FCSTD DOCUMENT  (FreeCAD 0.19R23578 (Git))
Label: frame_assembly
License: All rights reserved
LicenseURL: http://en.wikipedia.org/wiki/All_rights_reserved
objects: App::Link×11, App::DocumentObjectGroup×2, PartDesign::CoordinateSystem×1, App::FeaturePython×1, App::Part×1
note: 1 computed .brp shape members not serialized (recipe doc carries the construction recipe); baked Part::Feature solids carry a one-line shape summary decoded from their .brp
EXTERNAL_REF file=frame_bottom_piece.FCStd obj=LCS_4
EXTERNAL_REF file=frame_bottom_piece.FCStd obj=Part008
EXTERNAL_REF file=frame_bottom_piece.FCStd obj=LCS_2
EXTERNAL_REF file=frame_side_piece.FCStd obj=LCS_2
EXTERNAL_REF file=frame_side_piece.FCStd obj=Part006
EXTERNAL_REF file=frame_bottom_piece.FCStd obj=LCS_1
EXTERNAL_REF file=frame_side_piece.FCStd obj=LCS_1
EXTERNAL_REF file=frame_top_piece.FCStd obj=LCS_2
EXTERNAL_REF file=frame_top_piece.FCStd obj=Part007
EXTERNAL_REF file=frame_top_piece.FCStd obj=LCS_3
EXTERNAL_REF file=z_motor_adaptor_plate.FCStd obj=LCS_1
EXTERNAL_REF file=z_motor_adaptor_plate.FCStd obj=Part
EXTERNAL_REF file=Nema 17  Stepper Motor length 60mm.FcStd obj=LCS_0
EXTERNAL_REF file=z_motor_adaptor_plate.FCStd obj=LCS_2
EXTERNAL_REF file=Nema 17  Stepper Motor length 60mm.FcStd obj=Part
EXTERNAL_REF file=Nema 17  Stepper Motor length 60mm.FcStd obj=LCS_1
EXTERNAL_REF file=5to8mm_spider_coupler.FCStd obj=LCS_1
EXTERNAL_REF file=5to8mm_spider_coupler.FCStd obj=CouplerASM
EXTERNAL_REF file=T8_leadscrew_l388mm.FCStd obj=LCS_1
EXTERNAL_REF file=T8_leadscrew_l388mm.FCStd obj=Part
EXTERNAL_REF file=KLF08_bearing_block.FCStd obj=LCS_1
EXTERNAL_REF file=frame_bottom_piece.FCStd obj=LCS_3
EXTERNAL_REF file=KLF08_bearing_block.FCStd obj=Part
EXTERNAL_REF file=12x500mm_linear_shaft.FCStd obj=LCS_1
EXTERNAL_REF file=frame_bottom_piece.FCStd obj=LCS_5
EXTERNAL_REF file=12x500mm_linear_shaft.FCStd obj=Part
EXTERNAL_REF file=frame_bottom_piece.FCStd obj=LCS_6

FEATURE [App::DocumentObjectGroup] Parts
FEATURE [PartDesign::CoordinateSystem] LCS_Origin
  AttacherType = Attacher::AttachEngine3D
  MapMode = 2
  Support = -> [X_Axis]
FEATURE [App::DocumentObjectGroup] Constraints
FEATURE [App::FeaturePython] Variables  # WARN: FeaturePython — macro-defined, semantics opaque (R4)
FEATURE [App::Link] frame_bottom_piece_frame_bottom_piece
  AssemblyType = Asm4EE
  AttachedBy = #LCS_4
  AttachedTo = Parent Assembly#LCS_Origin
  LinkPlacement = pos=(-25.4,0,0) rot=(0,0,1;0rad)
  LinkedObject = -> <external frame_bottom_piece.FCStd>#Part008
  Placement = pos=(-25.4,0,0) rot=(0,0,1;0rad)
  expr: Placement = LCS_Origin.Placement * AttachmentOffset * frame_bottom_piece#LCS_4.Placement ^ -1
FEATURE [App::Link] frame_side_piece_frame_side_piece
  AssemblyType = Asm4EE
  AttachedBy = #LCS_2
  AttachedTo = frame_bottom_piece_frame_bottom_piece#LCS_2
  AttachmentOffset = pos=(0,0,0) rot=(1,0,0;4.71239rad)
  LinkPlacement = pos=(25.4,127,50.8) rot=(0,0,-1;4.71239rad)
  LinkedObject = -> <external frame_side_piece.FCStd>#Part006
  Placement = pos=(25.4,127,50.8) rot=(0,0,-1;4.71239rad)
  expr: Placement = frame_bottom_piece_frame_bottom_piece.Placement * frame_bottom_piece#LCS_2.Placement * AttachmentOffset * frame_side_piece#LCS_2.Placement ^ -1
FEATURE [App::Link] frame_side_piece_frame_side_piece_2
  AssemblyType = Asm4EE
  AttachedBy = #LCS_2
  AttachedTo = frame_bottom_piece_frame_bottom_piece#LCS_1
  AttachmentOffset = pos=(0,0,0) rot=(1,0,0;4.71239rad)
  LinkPlacement = pos=(25.4,-177.8,50.8) rot=(0,0,-1;4.71239rad)
  LinkedObject = -> <external frame_side_piece.FCStd>#Part006
  Placement = pos=(25.4,-177.8,50.8) rot=(0,0,-1;4.71239rad)
  expr: Placement = frame_bottom_piece_frame_bottom_piece.Placement * frame_bottom_piece#LCS_1.Placement * AttachmentOffset * frame_side_piece#LCS_2.Placement ^ -1
FEATURE [App::Link] frame_top_piece_frame_top_piece
  AssemblyType = Asm4EE
  AttachedBy = #LCS_2
  AttachedTo = frame_side_piece_frame_side_piece#LCS_1
  AttachmentOffset = pos=(0,0,0) rot=(1,0,0;1.5708rad)
  LinkPlacement = pos=(-25.4,-5.68e-14,449.2) rot=(0,0,1;0rad)
  LinkedObject = -> <external frame_top_piece.FCStd>#Part007
  Placement = pos=(-25.4,-5.68e-14,449.2) rot=(0,0,1;0rad)
  expr: Placement = frame_side_piece_frame_side_piece.Placement * frame_side_piece#LCS_1.Placement * AttachmentOffset * frame_top_piece#LCS_2.Placement ^ -1
FEATURE [App::Link] z_motor_adaptor_plate_z_motor_adaptor_plate
  AssemblyType = Asm4EE
  AttachedBy = #LCS_1
  AttachedTo = frame_top_piece_frame_top_piece#LCS_3
  AttachmentOffset = pos=(0,0,0) rot=(0,0,1;4.71239rad)
  LinkPlacement = pos=(-2.238e-13,-5.68e-14,500) rot=(0,0,-1;1.5708rad)
  LinkedObject = -> <external z_motor_adaptor_plate.FCStd>#Part
  Placement = pos=(-2.238e-13,-5.68e-14,500) rot=(0,0,-1;1.5708rad)
  expr: Placement = frame_top_piece_frame_top_piece.Placement * frame_top_piece#LCS_3.Placement * AttachmentOffset * z_motor_adaptor_plate#LCS_1.Placement ^ -1
FEATURE [App::Link] Nema_17__Stepper_Motor_length_60mm_Nema_17__Stepper_Motor_length_60mm  label="Nema_17__Stepper_Motor_length_60mm_Nema 17  Stepper Motor length 60mm"
  AssemblyType = Asm4EE
  AttachedBy = #LCS_0
  AttachedTo = z_motor_adaptor_plate_z_motor_adaptor_plate#LCS_2
  AttachmentOffset = pos=(0,0,0) rot=(1,0,0;3.14159rad)
  LinkPlacement = pos=(-2.804e-13,-6.32e-14,565.75) rot=(1,0,0;1.5708rad)
  LinkedObject = -> <external Nema 17  Stepper Motor length 60mm.FcStd>#Part
  Placement = pos=(-2.804e-13,-6.32e-14,565.75) rot=(1,0,0;1.5708rad)
  expr: Placement = z_motor_adaptor_plate_z_motor_adaptor_plate.Placement * z_motor_adaptor_plate#LCS_2.Placement * AttachmentOffset * Nema_17__Stepper_Motor_length_60mm#LCS_0.Placement ^ -1
FEATURE [App::Link] _to8mm_spider_coupler_5to8mm_spider_coupler
  AssemblyType = Asm4EE
  AttachedBy = #LCS_1
  AttachedTo = Nema_17__Stepper_Motor_length_60mm_Nema_17__Stepper_Motor_length_60mm#LCS_1
  AttachmentOffset = pos=(0,0,0) rot=(0,1,0;3.14159rad)
  LinkPlacement = pos=(-2.101e-13,-4.47e-14,497.15) rot=(-0.085794,-0.7045,0.7045;2.97042rad)
  LinkedObject = -> <external 5to8mm_spider_coupler.FCStd>#CouplerASM
  Placement = pos=(-2.101e-13,-4.47e-14,497.15) rot=(-0.085794,-0.7045,0.7045;2.97042rad)
  expr: Placement = Nema_17__Stepper_Motor_length_60mm_Nema_17__Stepper_Motor_length_60mm.Placement * Nema_17__Stepper_Motor_length_60mm#LCS_1.Placement * AttachmentOffset * _to8mm_spider_coupler#LCS_1.Placement ^ -1
FEATURE [App::Link] T8_leadscrew_l388mm_T8_leadscrew_l388mm
  AssemblyType = Asm4EE
  AttachedBy = #LCS_1
  AttachedTo = _to8mm_spider_coupler_5to8mm_spider_coupler#LCS_1
  AttachmentOffset = pos=(0,0,0) rot=(0,-1,0;3.14159rad)
  LinkPlacement = pos=(-2.051e-13,-4.55e-14,482.15) rot=(0.707107,0.707107,0;3.14159rad)
  LinkedObject = -> <external T8_leadscrew_l388mm.FCStd>#Part
  Placement = pos=(-2.051e-13,-4.55e-14,482.15) rot=(0.707107,0.707107,0;3.14159rad)
  expr: Placement = _to8mm_spider_coupler_5to8mm_spider_coupler.Placement * _to8mm_spider_coupler#LCS_1.Placement * AttachmentOffset * T8_leadscrew_l388mm#LCS_1.Placement ^ -1
FEATURE [App::Link] KLF08_bearing_block_KLF08
  AssemblyType = Asm4EE
  AttachedBy = #LCS_1
  AttachedTo = frame_bottom_piece_frame_bottom_piece#LCS_3
  AttachmentOffset = pos=(0,0,0) rot=(1,0,0;3.14159rad)
  LinkPlacement = pos=(0,0,50.8) rot=(0.57735,0.57735,0.57735;2.0944rad)
  LinkedObject = -> <external KLF08_bearing_block.FCStd>#Part
  Placement = pos=(0,0,50.8) rot=(0.57735,0.57735,0.57735;2.0944rad)
  expr: Placement = frame_bottom_piece_frame_bottom_piece.Placement * frame_bottom_piece#LCS_3.Placement * AttachmentOffset * KLF08_bearing_block#LCS_1.Placement ^ -1
FEATURE [App::Link] _2x500mm_linear_shaft_12x500mm_linear_shaft
  AssemblyType = Asm4EE
  AttachedBy = #LCS_1
  AttachedTo = frame_bottom_piece_frame_bottom_piece#LCS_5
  LinkPlacement = pos=(13.4,-95.25,0) rot=(0,0,-1;1.5708rad)
  LinkedObject = -> <external 12x500mm_linear_shaft.FCStd>#Part
  Placement = pos=(13.4,-95.25,0) rot=(0,0,-1;1.5708rad)
  expr: Placement = frame_bottom_piece_frame_bottom_piece.Placement * frame_bottom_piece#LCS_5.Placement * AttachmentOffset * _2x500mm_linear_shaft#LCS_1.Placement ^ -1
FEATURE [App::Link] _2x500mm_linear_shaft_12x500mm_linear_shaft_2
  AssemblyType = Asm4EE
  AttachedBy = #LCS_1
  AttachedTo = frame_bottom_piece_frame_bottom_piece#LCS_6
  LinkPlacement = pos=(13.4,95.25,0) rot=(0,0,-1;1.5708rad)
  LinkedObject = -> <external 12x500mm_linear_shaft.FCStd>#Part
  Placement = pos=(13.4,95.25,0) rot=(0,0,-1;1.5708rad)
  expr: Placement = frame_bottom_piece_frame_bottom_piece.Placement * frame_bottom_piece#LCS_6.Placement * AttachmentOffset * _2x500mm_linear_shaft#LCS_1.Placement ^ -1
FEATURE [App::Part] Model
  Configuration = 0
  Group = -> [LCS_Origin,Constraints,Variables,frame_bottom_piece_frame_bottom_piece,frame_side_piece_frame_side_piece,frame_side_piece_frame_side_piece_2,frame_top_piece_frame_top_piece,z_motor_adaptor_plate_z_motor_adaptor_plate,Nema_17__Stepper_Motor_length_60mm_Nema_17__Stepper_Motor_length_60mm,_to8mm_spider_coupler_5to8mm_spider_coupler,T8_leadscrew_l388mm_T8_leadscrew_l388mm,KLF08_bearing_block_KLF08,+2 more]
  Origin = -> Origin
  Type = Assembly4 Model

RESOLVED EXTERNAL PARTS (link-assembly join: the EXTERNAL_REF files above that resolve inside this repo's crawl, each included once):
---- part 12x500mm_linear_shaft.FCStd = doc fcstd_1ea531625638 ----
FCSTD DOCUMENT  (FreeCAD 0.19R23578 (Git))
Label: 12x500mm_linear_shaft
License: All rights reserved
LicenseURL: http://en.wikipedia.org/wiki/All_rights_reserved
objects: Sketcher::SketchObject×1, PartDesign::Pad×1, PartDesign::Chamfer×1, PartDesign::Body×1, PartDesign::CoordinateSystem×1, App::Part×1
note: 7 computed .brp shape members not serialized (recipe doc carries the construction recipe); baked Part::Feature solids carry a one-line shape summary decoded from their .brp

FEATURE [Sketcher::SketchObject] Sketch
  MapMode = 5
  Support = -> [XY_Plane001]
  sketch-geometry (1):
    g0: Circle CenterX=0 CenterY=0 CenterZ=0 NormalX=0 NormalY=0 NormalZ=1 AngleXU=0 Radius=6
  constraints (2):
    c: Coincident(g0,g-1)
    c: Diameter(g0) = 12
FEATURE [PartDesign::Pad] Pad
  Direction = (1,1,1)
  Length = 500
  Length2 = 100
  Profile = -> Sketch
  Type = 0
FEATURE [PartDesign::Chamfer] Chamfer
  Angle = 45
  Base = -> Pad [Edge2,Edge3]
  BaseFeature = -> Pad
  ChamferType = 0
  FlipDirection = false
  Size = 1
  Size2 = 1
  SupportTransform = true
FEATURE [PartDesign::Body] Body
  Group = -> [Sketch,Pad,Chamfer]
  Origin = -> Origin001
  Tip = -> Chamfer
FEATURE [PartDesign::CoordinateSystem] LCS_1
  AttacherType = Attacher::AttachEngine3D
  MapMode = 11
  Placement = pos=(0,0,0) rot=(0,0,1;1.5708rad)
  Support = -> [Chamfer]
FEATURE [App::Part] Part  label="12x500mm_linear_shaft"
  Group = -> [Body,LCS_1]
  Origin = -> Origin
---- part T8_leadscrew_l388mm.FCStd = doc fcstd_92d1f95667da ----
FCSTD DOCUMENT  (FreeCAD 0.19R23578 (Git))
Label: T8_leadscrew_l388mm
License: All rights reserved
LicenseURL: http://en.wikipedia.org/wiki/All_rights_reserved
objects: PartDesign::CoordinateSystem×2, Sketcher::SketchObject×1, PartDesign::Pad×1, PartDesign::Chamfer×1, PartDesign::Body×1, App::Part×1
note: 8 computed .brp shape members not serialized (recipe doc carries the construction recipe); baked Part::Feature solids carry a one-line shape summary decoded from their .brp

FEATURE [Sketcher::SketchObject] Sketch
  MapMode = 5
  Support = -> [XY_Plane001]
  sketch-geometry (1):
    g0: Circle CenterX=0 CenterY=0 CenterZ=0 NormalX=0 NormalY=0 NormalZ=1 AngleXU=0 Radius=4
  constraints (2):
    c: Coincident(g0,g-1)
    c: Diameter(g0) = 8
FEATURE [PartDesign::Pad] Pad
  Direction = (1,1,1)
  Length = 433
  Length2 = 100
  Profile = -> Sketch
  Type = 0
FEATURE [PartDesign::Chamfer] Chamfer
  Angle = 45
  Base = -> Pad [Edge2,Edge3]
  BaseFeature = -> Pad
  ChamferType = 0
  FlipDirection = false
  Size = 1
  Size2 = 1
  SupportTransform = true
FEATURE [PartDesign::Body] Body
  Group = -> [Sketch,Pad,Chamfer]
  Origin = -> Origin001
  Tip = -> Chamfer
FEATURE [PartDesign::CoordinateSystem] LCS_1
  AttacherType = Attacher::AttachEngine3D
  MapMode = 11
  Placement = pos=(0,0,0) rot=(0,0,1;1.5708rad)
  Support = -> [Chamfer]
FEATURE [PartDesign::CoordinateSystem] LCS_2
  AttacherType = Attacher::AttachEngine3D
  MapMode = 45
  Placement = pos=(-9e-16,-1e-16,216.5) rot=(0,0,1;0rad)
  Support = -> [Chamfer]
FEATURE [App::Part] Part  label="T8_leadscrew_l388mm"
  Group = -> [Body,LCS_1,LCS_2]
  Origin = -> Origin
---- part frame_bottom_piece.FCStd = doc fcstd_ccebaa61afa7 ----
FCSTD DOCUMENT  (FreeCAD 0.19R23578 (Git))
Label: frame_bottom_piece
License: All rights reserved
LicenseURL: http://en.wikipedia.org/wiki/All_rights_reserved
objects: PartDesign::CoordinateSystem×6, Sketcher::SketchObject×4, PartDesign::Pocket×3, PartDesign::Pad×1, PartDesign::Body×1, App::Part×1
note: 19 computed .brp shape members not serialized (recipe doc carries the construction recipe); baked Part::Feature solids carry a one-line shape summary decoded from their .brp

FEATURE [Sketcher::SketchObject] Sketch006
  AttachmentOffset = pos=(0,0,50.8) rot=(0,0,1;0rad)
  MapMode = 5
  Placement = pos=(50.8,-1.13e-14,1.13e-14) rot=(0.57735,0.57735,0.57735;2.0944rad)
  Support = -> [YZ_Plane011]
  sketch-geometry (8):
    g0: ArcOfCircle CenterX=-131 CenterY=25.4 CenterZ=0 NormalX=0 NormalY=0 NormalZ=1 AngleXU=0 Radius=5 StartAngle=1.5708 EndAngle=4.71239
    g1: ArcOfCircle CenterX=-95 CenterY=25.4 CenterZ=0 NormalX=0 NormalY=0 NormalZ=1 AngleXU=0 Radius=5 StartAngle=4.71239 EndAngle=7.85398
    g2: LineSegment StartX=-131 StartY=20.4 StartZ=0 EndX=-95 EndY=20.4 EndZ=0
    g3: LineSegment StartX=-131 StartY=30.4 StartZ=0 EndX=-95 EndY=30.4 EndZ=0
    g4: ArcOfCircle CenterX=95 CenterY=25.4 CenterZ=0 NormalX=0 NormalY=0 NormalZ=1 AngleXU=0 Radius=5 StartAngle=1.5708 EndAngle=4.71239
    g5: ArcOfCircle CenterX=131 CenterY=25.4 CenterZ=0 NormalX=0 NormalY=0 NormalZ=1 AngleXU=0 Radius=5 StartAngle=4.71239 EndAngle=7.85398
    g6: LineSegment StartX=95 StartY=20.4 StartZ=0 EndX=131 EndY=20.4 EndZ=0
    g7: LineSegment StartX=95 StartY=30.4 StartZ=0 EndX=131 EndY=30.4 EndZ=0
  constraints (18):
    c: Tangent(g0,g3) = 1.5708
    c: Tangent(g0,g2) = -1.5708
    c: Tangent(g2,g1) = -1.5708
    c: Tangent(g3,g1) = 1.5708
    c: Horizontal(g2)
    c: Equal(g0,g1)
    c: Tangent(g4,g7) = 1.5708
    c: Tangent(g4,g6) = -1.5708
    c: Tangent(g6,g5) = -1.5708
    c: Tangent(g7,g5) = 1.5708
    c: Horizontal(g6)
    c: Diameter(g4) = 10
    c: Equal(g4,g1)
    c: Symmetric(g4,g1,g-2)
    c: Symmetric(g0,g5,g-2)
    c: DistanceY(g-1,g4) = 25.4
    c: DistanceX(g1,g4) = 190
    c: DistanceX(g0,g5) = 262
FEATURE [Sketcher::SketchObject] Sketch012
  AttachmentOffset = pos=(0,0,50.8) rot=(0,0,1;0rad)
  MapMode = 5
  Placement = pos=(0,0,50.8) rot=(0,0,1;0rad)
  Support = -> [XY_Plane011]
  sketch-geometry (4):
    g0: Circle CenterX=25.4 CenterY=0 CenterZ=0 NormalX=0 NormalY=0 NormalZ=1 AngleXU=0 Radius=9
    g1: Circle CenterX=25.4 CenterY=18.5 CenterZ=0 NormalX=0 NormalY=0 NormalZ=1 AngleXU=0 Radius=2.25
    g2: Circle CenterX=25.4 CenterY=-18.5 CenterZ=0 NormalX=0 NormalY=0 NormalZ=1 AngleXU=0 Radius=2.25
    g3: LineSegment StartX=25.4 StartY=18.5 StartZ=0 EndX=25.4 EndY=-18.5 EndZ=0
  constraints (10):
    c: PointOnObject(g0,g-1)
    c: Coincident(g3,g1)
    c: Coincident(g3,g2)
    c: PointOnObject(g0,g3)
    c: Symmetric(g1,g2,g-1)
    c: Equal(g1,g2)
    c: DistanceY(g2,g1) = 37
    c: DistanceX(g-1,g0) = 25.4
    c: Diameter(g1) = 4.5
    c: Diameter(g0) = 18
FEATURE [Sketcher::SketchObject] Sketch
  MapMode = 5
  Placement = pos=(0,0,0) rot=(1,0,0;1.5708rad)
  Support = -> [XZ_Plane011]
  sketch-geometry (16):
    g0: LineSegment StartX=10 StartY=0 StartZ=0 EndX=40.8 EndY=0 EndZ=0
    g1: LineSegment StartX=50.8 StartY=10 StartZ=0 EndX=50.8 EndY=40.8 EndZ=0
    g2: LineSegment StartX=40.8 StartY=50.8 StartZ=0 EndX=10 EndY=50.8 EndZ=0
    g3: LineSegment StartX=0 StartY=40.8 StartZ=0 EndX=0 EndY=10 EndZ=0
    g4: ArcOfCircle CenterX=10 CenterY=40.8 CenterZ=0 NormalX=0 NormalY=0 NormalZ=1 AngleXU=0 Radius=10 StartAngle=1.5708 EndAngle=3.14159
    g5: ArcOfCircle CenterX=10 CenterY=10 CenterZ=0 NormalX=0 NormalY=0 NormalZ=1 AngleXU=0 Radius=10 StartAngle=3.14159 EndAngle=4.71239
    g6: ArcOfCircle CenterX=40.8 CenterY=10 CenterZ=0 NormalX=0 NormalY=0 NormalZ=1 AngleXU=0 Radius=10 StartAngle=4.71239 EndAngle=6.28319
    g7: ArcOfCircle CenterX=40.8 CenterY=40.8 CenterZ=0 NormalX=0 NormalY=0 NormalZ=1 AngleXU=0 Radius=10 StartAngle=3e-16 EndAngle=1.5708
    g8: LineSegment StartX=10 StartY=46.0375 StartZ=0 EndX=40.8 EndY=46.0375 EndZ=0
    g9: LineSegment StartX=46.0375 StartY=40.8 StartZ=0 EndX=46.0375 EndY=10 EndZ=0
    g10: LineSegment StartX=40.8 StartY=4.7625 StartZ=0 EndX=10 EndY=4.7625 EndZ=0
    g11: LineSegment StartX=4.7625 StartY=10 StartZ=0 EndX=4.7625 EndY=40.8 EndZ=0
    g12: ArcOfCircle CenterX=10 CenterY=40.8 CenterZ=0 NormalX=0 NormalY=0 NormalZ=1 AngleXU=0 Radius=5.2375 StartAngle=1.5708 EndAngle=3.14159
    g13: ArcOfCircle CenterX=10 CenterY=10 CenterZ=0 NormalX=0 NormalY=0 NormalZ=1 AngleXU=0 Radius=5.2375 StartAngle=3.14159 EndAngle=4.71239
    g14: ArcOfCircle CenterX=40.8 CenterY=10 CenterZ=0 NormalX=0 NormalY=0 NormalZ=1 AngleXU=0 Radius=5.2375 StartAngle=4.71239 EndAngle=6.28319
    g15: ArcOfCircle CenterX=40.8 CenterY=40.8 CenterZ=0 NormalX=0 NormalY=0 NormalZ=1 AngleXU=0 Radius=5.2375 StartAngle=0 EndAngle=1.5708
  constraints (36):
    c: Horizontal(g0)
    c: Horizontal(g2)
    c: Vertical(g1)
    c: Vertical(g3)
    c: Tangent(g2,g4) = -1.5708
    c: Tangent(g3,g4) = -1.5708
    c: Tangent(g3,g5) = -1.5708
    c: Tangent(g0,g5) = -1.5708
    c: Tangent(g0,g6) = -1.5708
    c: Tangent(g1,g6) = -1.5708
    c: Tangent(g2,g7) = -1.5708
    c: Tangent(g1,g7) = -1.5708
    c: Horizontal(g8)
    c: Horizontal(g10)
    c: Vertical(g9)
    c: Tangent(g8,g12) = 1.5708
    c: Tangent(g11,g12) = 1.5708
    c: Tangent(g11,g13) = 1.5708
    c: Tangent(g10,g13) = 1.5708
    c: Tangent(g9,g14) = 1.5708
    c: Tangent(g10,g14) = 1.5708
    c: Tangent(g8,g15) = 1.5708
    c: Tangent(g9,g15) = 1.5708
    c: PointOnObject(g3,g-2)
    c: PointOnObject(g0,g-1)
    c: DistanceX(g3,g1) = 50.8
    c: DistanceY(g0,g2) = 50.8
    c: Coincident(g13,g5)
    c: Coincident(g12,g4)
    c: Coincident(g7,g15)
    c: Coincident(g14,g6)
    c: Equal(g5,g4)
    c: Equal(g4,g7)
    c: Equal(g7,g6)
    c: DistanceX(g3,g11) = 4.7625
    c: DistanceX(g3,g0) = 10
FEATURE [PartDesign::Pad] Pad
  AllowMultiFace = false
  Direction = (1,1,1)
  Length = 355.6
  Length2 = 100
  Midplane = true
  Placement = pos=(0,0,0) rot=(1,0,0;1.5708rad)
  Profile = -> Sketch
  Type = 0
FEATURE [Sketcher::SketchObject] Sketch005
  AttachmentOffset = pos=(0,0,50.8) rot=(0,0,1;0rad)
  MapMode = 5
  Placement = pos=(0,0,50.8) rot=(0,0,1;0rad)
  Support = -> [XY_Plane011]
  sketch-geometry (8):
    g0: LineSegment StartX=32.8 StartY=89.25 StartZ=0 EndX=57.8 EndY=89.25 EndZ=0
    g1: LineSegment StartX=57.8 StartY=89.25 StartZ=0 EndX=57.8 EndY=109.25 EndZ=0
    g2: LineSegment StartX=57.8 StartY=109.25 StartZ=0 EndX=32.8 EndY=109.25 EndZ=0
    g3: LineSegment StartX=32.8 StartY=109.25 StartZ=0 EndX=32.8 EndY=89.25 EndZ=0
    g4: LineSegment StartX=32.8 StartY=-89.25 StartZ=0 EndX=57.8 EndY=-89.25 EndZ=0
    g5: LineSegment StartX=57.8 StartY=-89.25 StartZ=0 EndX=57.8 EndY=-109.25 EndZ=0
    g6: LineSegment StartX=57.8 StartY=-109.25 StartZ=0 EndX=32.8 EndY=-109.25 EndZ=0
    g7: LineSegment StartX=32.8 StartY=-109.25 StartZ=0 EndX=32.8 EndY=-89.25 EndZ=0
  constraints (22):
    c: Coincident(g0,g1)
    c: Coincident(g1,g2)
    c: Coincident(g2,g3)
    c: Coincident(g3,g0)
    c: Horizontal(g0)
    c: Horizontal(g2)
    c: Vertical(g1)
    c: Vertical(g3)
    c: Coincident(g4,g5)
    c: Coincident(g5,g6)
    c: Coincident(g6,g7)
    c: Coincident(g7,g4)
    c: Horizontal(g4)
    c: Horizontal(g6)
    c: Vertical(g5)
    c: Vertical(g7)
    c: Symmetric(g0,g4,g-1)
    c: Symmetric(g1,g5,g-1)
    c: DistanceY(g1,g1) = 20
    c: DistanceX(g-1,g0) = 32.8
    c: DistanceX(g0,g0) = 25
    c: DistanceY(g4,g0) = 178.5
FEATURE [PartDesign::Pocket] Pocket
  AllowMultiFace = false
  BaseFeature = -> Pad
  Length = 5
  Length2 = 100
  Placement = pos=(0,0,0) rot=(1,0,0;1.5708rad)
  Profile = -> Sketch005
  Type = 1
FEATURE [PartDesign::Pocket] Pocket001
  AllowMultiFace = false
  BaseFeature = -> Pocket
  Length = 5
  Length2 = 100
  Placement = pos=(0,0,0) rot=(1,0,0;1.5708rad)
  Profile = -> Sketch006
  Type = 2
FEATURE [PartDesign::Pocket] Pocket006
  AllowMultiFace = false
  BaseFeature = -> Pocket001
  Length = 5
  Length2 = 100
  Placement = pos=(0,0,0) rot=(1,0,0;1.5708rad)
  Profile = -> Sketch012
  Type = 0
FEATURE [PartDesign::Body] Body
  Group = -> [Sketch,Pad,Sketch005,Pocket,Sketch006,Pocket001,Sketch012,Pocket006]
  Origin = -> Origin011
  Tip = -> Pocket006
FEATURE [PartDesign::CoordinateSystem] LCS_1
  AttacherType = Attacher::AttachEngine3D
  AttachmentOffset = pos=(25.4,0,0) rot=(0,0,1;0rad)
  MapMode = 45
  Placement = pos=(25.4,-152.4,50.8) rot=(0.57735,0.57735,0.57735;2.0944rad)
  Support = -> [Pocket006]
  expr: .AttachmentOffset.Base.x = 1"
FEATURE [PartDesign::CoordinateSystem] LCS_2
  AttacherType = Attacher::AttachEngine3D
  AttachmentOffset = pos=(-25.4,0,0) rot=(0,0,1;0rad)
  MapMode = 45
  Placement = pos=(25.4,152.4,50.8) rot=(0.57735,0.57735,0.57735;2.0944rad)
  Support = -> [Pocket006]
  expr: .AttachmentOffset.Base.x = -1"
FEATURE [PartDesign::CoordinateSystem] LCS_3
  AttacherType = Attacher::AttachEngine3D
  MapMode = 11
  Placement = pos=(25.4,0,50.8) rot=(0,0,1;1.5708rad)
  Support = -> [Pocket006]
FEATURE [PartDesign::CoordinateSystem] LCS_4
  AttacherType = Attacher::AttachEngine3D
  MapMode = 45
  Placement = pos=(25.4,0,0) rot=(0,0,1;0rad)
  Support = -> [Pocket006]
FEATURE [PartDesign::CoordinateSystem] LCS_5
  AttacherType = Attacher::AttachEngine3D
  AttachmentOffset = pos=(6,-6,0) rot=(0,0,1;0rad)
  MapMode = 1
  Placement = pos=(38.8,-95.25,0) rot=(0,0,1;0rad)
  Support = -> [Pocket006]
FEATURE [PartDesign::CoordinateSystem] LCS_6
  AttacherType = Attacher::AttachEngine3D
  AttachmentOffset = pos=(6,6,0) rot=(0,0,1;0rad)
  MapMode = 1
  Placement = pos=(38.8,95.25,0) rot=(0,0,1;0rad)
  Support = -> [Pocket006]
FEATURE [App::Part] Part008  label="frame_bottom_piece"
  Group = -> [Body,LCS_1,LCS_2,LCS_3,LCS_4,LCS_5,LCS_6]
  Origin = -> Origin009
---- part frame_side_piece.FCStd = doc fcstd_32cf0ac6b02a ----
FCSTD DOCUMENT  (FreeCAD 0.19R23578 (Git))
Label: frame_side_piece
License: All rights reserved
LicenseURL: http://en.wikipedia.org/wiki/All_rights_reserved
objects: PartDesign::CoordinateSystem×2, Sketcher::SketchObject×1, PartDesign::Pad×1, PartDesign::Body×1, App::Part×1
note: 6 computed .brp shape members not serialized (recipe doc carries the construction recipe); baked Part::Feature solids carry a one-line shape summary decoded from their .brp

FEATURE [Sketcher::SketchObject] Sketch004
  MapMode = 5
  sketch-geometry (16):
    g0: LineSegment StartX=10 StartY=0 StartZ=0 EndX=40.8 EndY=0 EndZ=0
    g1: LineSegment StartX=50.8 StartY=10 StartZ=0 EndX=50.8 EndY=40.8 EndZ=0
    g2: LineSegment StartX=40.8 StartY=50.8 StartZ=0 EndX=10 EndY=50.8 EndZ=0
    g3: LineSegment StartX=0 StartY=40.8 StartZ=0 EndX=0 EndY=10 EndZ=0
    g4: ArcOfCircle CenterX=10 CenterY=40.8 CenterZ=0 NormalX=0 NormalY=0 NormalZ=1 AngleXU=0 Radius=10 StartAngle=1.5708 EndAngle=3.14159
    g5: ArcOfCircle CenterX=10 CenterY=10 CenterZ=0 NormalX=0 NormalY=0 NormalZ=1 AngleXU=0 Radius=10 StartAngle=3.14159 EndAngle=4.71239
    g6: ArcOfCircle CenterX=40.8 CenterY=10 CenterZ=0 NormalX=0 NormalY=0 NormalZ=1 AngleXU=0 Radius=10 StartAngle=4.71239 EndAngle=6.28319
    g7: ArcOfCircle CenterX=40.8 CenterY=40.8 CenterZ=0 NormalX=0 NormalY=0 NormalZ=1 AngleXU=0 Radius=10 StartAngle=0 EndAngle=1.5708
    g8: LineSegment StartX=10 StartY=46.0375 StartZ=0 EndX=40.8 EndY=46.0375 EndZ=0
    g9: LineSegment StartX=46.0375 StartY=40.8 StartZ=0 EndX=46.0375 EndY=10 EndZ=0
    g10: LineSegment StartX=40.8 StartY=4.7625 StartZ=0 EndX=10 EndY=4.7625 EndZ=0
    g11: LineSegment StartX=4.7625 StartY=10 StartZ=0 EndX=4.7625 EndY=40.8 EndZ=0
    g12: ArcOfCircle CenterX=10 CenterY=40.8 CenterZ=0 NormalX=0 NormalY=0 NormalZ=1 AngleXU=0 Radius=5.2375 StartAngle=1.5708 EndAngle=3.14159
    g13: ArcOfCircle CenterX=10 CenterY=10 CenterZ=0 NormalX=0 NormalY=0 NormalZ=1 AngleXU=0 Radius=5.2375 StartAngle=3.14159 EndAngle=4.71239
    g14: ArcOfCircle CenterX=40.8 CenterY=10 CenterZ=0 NormalX=0 NormalY=0 NormalZ=1 AngleXU=0 Radius=5.2375 StartAngle=4.71239 EndAngle=6.28319
    g15: ArcOfCircle CenterX=40.8 CenterY=40.8 CenterZ=0 NormalX=0 NormalY=0 NormalZ=1 AngleXU=0 Radius=5.2375 StartAngle=4e-16 EndAngle=1.5708
  constraints (36):
    c: Horizontal(g0)
    c: Horizontal(g2)
    c: Vertical(g1)
    c: Vertical(g3)
    c: Tangent(g2,g4) = -1.5708
    c: Tangent(g3,g4) = -1.5708
    c: Tangent(g3,g5) = -1.5708
    c: Tangent(g0,g5) = -1.5708
    c: Tangent(g0,g6) = -1.5708
    c: Tangent(g1,g6) = -1.5708
    c: Tangent(g2,g7) = -1.5708
    c: Tangent(g1,g7) = -1.5708
    c: Horizontal(g8)
    c: Horizontal(g10)
    c: Vertical(g9)
    c: Tangent(g8,g12) = 1.5708
    c: Tangent(g11,g12) = 1.5708
    c: Tangent(g11,g13) = 1.5708
    c: Tangent(g10,g13) = 1.5708
    c: Tangent(g9,g14) = 1.5708
    c: Tangent(g10,g14) = 1.5708
    c: Tangent(g8,g15) = 1.5708
    c: Tangent(g9,g15) = 1.5708
    c: PointOnObject(g3,g-2)
    c: PointOnObject(g0,g-1)
    c: DistanceX(g3,g1) = 50.8
    c: DistanceY(g0,g2) = 50.8
    c: Coincident(g13,g5)
    c: Coincident(g12,g4)
    c: Coincident(g7,g15)
    c: Coincident(g14,g6)
    c: Equal(g5,g4)
    c: Equal(g4,g7)
    c: Equal(g7,g6)
    c: DistanceX(g3,g0) = 10
    c: DistanceX(g9,g1) = 4.7625
FEATURE [PartDesign::Pad] Pad004
  AllowMultiFace = false
  Direction = (1,1,1)
  Length = 398.4
  Length2 = 100
  Profile = -> Sketch004
  Type = 0
FEATURE [PartDesign::Body] Body004
  Group = -> [Sketch004,Pad004]
  Tip = -> Pad004
FEATURE [PartDesign::CoordinateSystem] LCS_1
  AttacherType = Attacher::AttachEngine3D
  MapMode = 45
  Placement = pos=(25.4,25.4,398.4) rot=(0,0,1;0rad)
  Support = -> [Pad004]
FEATURE [PartDesign::CoordinateSystem] LCS_2
  AttacherType = Attacher::AttachEngine3D
  MapMode = 45
  Placement = pos=(25.4,25.4,0) rot=(0,0,1;0rad)
  Support = -> [Pad004]
FEATURE [App::Part] Part006  label="frame_side_piece"
  Group = -> [Body004,LCS_1,LCS_2]
  Origin = -> Origin007
---- part frame_top_piece.FCStd = doc fcstd_cebd3a7141f0 ----
FCSTD DOCUMENT  (FreeCAD 0.19R23578 (Git))
Label: frame_top_piece
License: All rights reserved
LicenseURL: http://en.wikipedia.org/wiki/All_rights_reserved
objects: Sketcher::SketchObject×5, PartDesign::Pocket×4, PartDesign::CoordinateSystem×3, PartDesign::Pad×1, PartDesign::Body×1, App::Part×1
note: 19 computed .brp shape members not serialized (recipe doc carries the construction recipe); baked Part::Feature solids carry a one-line shape summary decoded from their .brp

FEATURE [Sketcher::SketchObject] Sketch010
  AttachmentOffset = pos=(0,0,50.8) rot=(0,0,1;0rad)
  MapMode = 5
  Placement = pos=(0,0,50.8) rot=(0,0,1;0rad)
  Support = -> [XY_Plane010]
  expr: Constraints[9] = (2 * 31 ^ 2) ^ 0.5
  sketch-geometry (4):
    g0: Circle CenterX=25.4 CenterY=0 CenterZ=0 NormalX=0 NormalY=0 NormalZ=1 AngleXU=0 Radius=11
    g1: Circle CenterX=25.4 CenterY=21.9203 CenterZ=0 NormalX=0 NormalY=0 NormalZ=1 AngleXU=0 Radius=1.55
    g2: Circle CenterX=25.4 CenterY=-21.9203 CenterZ=0 NormalX=0 NormalY=0 NormalZ=1 AngleXU=0 Radius=1.55
    g3: LineSegment StartX=25.4 StartY=21.9203 StartZ=0 EndX=25.4 EndY=-21.9203 EndZ=0
  constraints (10):
    c: PointOnObject(g0,g-1)
    c: Coincident(g3,g1)
    c: Coincident(g3,g2)
    c: DistanceX(g-1,g0) = 25.4
    c: PointOnObject(g0,g3)
    c: Symmetric(g1,g2,g-1)
    c: Equal(g1,g2)
    c: Diameter(g1) = 3.1
    c: Diameter(g0) = 22
    c: DistanceY(g2,g1) = 43.8406
FEATURE [Sketcher::SketchObject] Sketch011
  MapMode = 5
  Placement = pos=(0,0,0) rot=(0.57735,0.57735,0.57735;2.0944rad)
  Support = -> [YZ_Plane008]
  sketch-geometry (4):
    g0: LineSegment StartX=-20 StartY=20 StartZ=0 EndX=20 EndY=20 EndZ=0
    g1: LineSegment StartX=20 StartY=20 StartZ=0 EndX=20 EndY=-5 EndZ=0
    g2: LineSegment StartX=20 StartY=-5 StartZ=0 EndX=-20 EndY=-5 EndZ=0
    g3: LineSegment StartX=-20 StartY=-5 StartZ=0 EndX=-20 EndY=20 EndZ=0
  constraints (12):
    c: Coincident(g0,g1)
    c: Coincident(g1,g2)
    c: Coincident(g2,g3)
    c: Coincident(g3,g0)
    c: Horizontal(g0)
    c: Horizontal(g2)
    c: Vertical(g1)
    c: Vertical(g3)
    c: DistanceX(g0,g0) = 40
    c: DistanceY(g1,g0) = 25
    c: DistanceY(g-1,g0) = 20
    c: DistanceX(g-1,g0) = 20
FEATURE [Sketcher::SketchObject] Sketch007
  AttachmentOffset = pos=(0,0,50.8) rot=(0,0,1;0rad)
  MapMode = 5
  Placement = pos=(0,0,50.8) rot=(0,0,1;0rad)
  Support = -> [XY_Plane010]
  sketch-geometry (8):
    g0: LineSegment StartX=32.8 StartY=89.25 StartZ=0 EndX=57.8 EndY=89.25 EndZ=0
    g1: LineSegment StartX=57.8 StartY=89.25 StartZ=0 EndX=57.8 EndY=113.05 EndZ=0
    g2: LineSegment StartX=57.8 StartY=113.05 StartZ=0 EndX=32.8 EndY=113.05 EndZ=0
    g3: LineSegment StartX=32.8 StartY=113.05 StartZ=0 EndX=32.8 EndY=89.25 EndZ=0
    g4: LineSegment StartX=32.8 StartY=-89.25 StartZ=0 EndX=57.8 EndY=-89.25 EndZ=0
    g5: LineSegment StartX=57.8 StartY=-89.25 StartZ=0 EndX=57.8 EndY=-113.05 EndZ=0
    g6: LineSegment StartX=57.8 StartY=-113.05 StartZ=0 EndX=32.8 EndY=-113.05 EndZ=0
    g7: LineSegment StartX=32.8 StartY=-113.05 StartZ=0 EndX=32.8 EndY=-89.25 EndZ=0
  constraints (22):
    c: Coincident(g0,g1)
    c: Coincident(g1,g2)
    c: Coincident(g2,g3)
    c: Coincident(g3,g0)
    c: Horizontal(g0)
    c: Horizontal(g2)
    c: Vertical(g1)
    c: Vertical(g3)
    c: Coincident(g4,g5)
    c: Coincident(g5,g6)
    c: Coincident(g6,g7)
    c: Coincident(g7,g4)
    c: Horizontal(g4)
    c: Horizontal(g6)
    c: Vertical(g5)
    c: Vertical(g7)
    c: Symmetric(g0,g4,g-1)
    c: Symmetric(g1,g5,g-1)
    c: DistanceY(g1,g1) = 23.8
    c: DistanceX(g-1,g0) = 32.8
    c: DistanceX(g0,g0) = 25
    c: DistanceY(g4,g0) = 178.5
FEATURE [Sketcher::SketchObject] Sketch008
  MapMode = 5
  Placement = pos=(0,0,0) rot=(1,0,0;1.5708rad)
  Support = -> [XZ_Plane008]
  sketch-geometry (16):
    g0: LineSegment StartX=10 StartY=1.8e-15 StartZ=0 EndX=40.8 EndY=1.8e-15 EndZ=0
    g1: LineSegment StartX=50.8 StartY=10 StartZ=0 EndX=50.8 EndY=40.8 EndZ=0
    g2: LineSegment StartX=40.8 StartY=50.8 StartZ=0 EndX=10 EndY=50.8 EndZ=0
    g3: LineSegment StartX=0 StartY=40.8 StartZ=0 EndX=0 EndY=10 EndZ=0
    g4: ArcOfCircle CenterX=10 CenterY=40.8 CenterZ=0 NormalX=0 NormalY=0 NormalZ=1 AngleXU=0 Radius=10 StartAngle=1.5708 EndAngle=3.14159
    g5: ArcOfCircle CenterX=10 CenterY=10 CenterZ=0 NormalX=0 NormalY=0 NormalZ=1 AngleXU=0 Radius=10 StartAngle=3.14159 EndAngle=4.71239
    g6: ArcOfCircle CenterX=40.8 CenterY=10 CenterZ=0 NormalX=0 NormalY=0 NormalZ=1 AngleXU=0 Radius=10 StartAngle=4.71239 EndAngle=6.28319
    g7: ArcOfCircle CenterX=40.8 CenterY=40.8 CenterZ=0 NormalX=0 NormalY=0 NormalZ=1 AngleXU=0 Radius=10 StartAngle=3e-16 EndAngle=1.5708
    g8: LineSegment StartX=10 StartY=46.0375 StartZ=0 EndX=40.8 EndY=46.0375 EndZ=0
    g9: LineSegment StartX=46.0375 StartY=40.8 StartZ=0 EndX=46.0375 EndY=10 EndZ=0
    g10: LineSegment StartX=40.8 StartY=4.7625 StartZ=0 EndX=10 EndY=4.7625 EndZ=0
    g11: LineSegment StartX=4.7625 StartY=10 StartZ=0 EndX=4.7625 EndY=40.8 EndZ=0
    g12: ArcOfCircle CenterX=10 CenterY=40.8 CenterZ=0 NormalX=0 NormalY=0 NormalZ=1 AngleXU=0 Radius=5.2375 StartAngle=1.5708 EndAngle=3.14159
    g13: ArcOfCircle CenterX=10 CenterY=10 CenterZ=0 NormalX=0 NormalY=0 NormalZ=1 AngleXU=0 Radius=5.2375 StartAngle=3.14159 EndAngle=4.71239
    g14: ArcOfCircle CenterX=40.8 CenterY=10 CenterZ=0 NormalX=0 NormalY=0 NormalZ=1 AngleXU=0 Radius=5.2375 StartAngle=4.71239 EndAngle=6.28319
    g15: ArcOfCircle CenterX=40.8 CenterY=40.8 CenterZ=0 NormalX=0 NormalY=0 NormalZ=1 AngleXU=0 Radius=5.2375 StartAngle=0 EndAngle=1.5708
  constraints (36):
    c: Horizontal(g0)
    c: Horizontal(g2)
    c: Vertical(g1)
    c: Vertical(g3)
    c: Tangent(g2,g4) = -1.5708
    c: Tangent(g3,g4) = -1.5708
    c: Tangent(g3,g5) = -1.5708
    c: Tangent(g0,g5) = -1.5708
    c: Tangent(g0,g6) = -1.5708
    c: Tangent(g1,g6) = -1.5708
    c: Tangent(g2,g7) = -1.5708
    c: Tangent(g1,g7) = -1.5708
    c: Horizontal(g8)
    c: Horizontal(g10)
    c: Vertical(g9)
    c: Tangent(g8,g12) = 1.5708
    c: Tangent(g11,g12) = 1.5708
    c: Tangent(g11,g13) = 1.5708
    c: Tangent(g10,g13) = 1.5708
    c: Tangent(g9,g14) = 1.5708
    c: Tangent(g10,g14) = 1.5708
    c: Tangent(g8,g15) = 1.5708
    c: Tangent(g9,g15) = 1.5708
    c: PointOnObject(g3,g-2)
    c: PointOnObject(g0,g-1)
    c: DistanceX(g3,g1) = 50.8
    c: DistanceY(g0,g2) = 50.8
    c: Coincident(g13,g5)
    c: Coincident(g12,g4)
    c: Coincident(g7,g15)
    c: Coincident(g14,g6)
    c: Equal(g5,g4)
    c: Equal(g4,g7)
    c: Equal(g7,g6)
    c: DistanceX(g3,g11) = 4.7625
    c: DistanceX(g3,g0) = 10
FEATURE [PartDesign::Pad] Pad005
  AllowMultiFace = false
  Direction = (1,1,1)
  Length = 355.6
  Length2 = 100
  Midplane = true
  Placement = pos=(0,0,0) rot=(1,0,0;1.5708rad)
  Profile = -> Sketch008
  Type = 0
FEATURE [PartDesign::Pocket] Pocket002
  AllowMultiFace = false
  BaseFeature = -> Pad005
  Length = 5
  Length2 = 100
  Placement = pos=(0,0,0) rot=(1,0,0;1.5708rad)
  Profile = -> Sketch007
  Type = 1
FEATURE [Sketcher::SketchObject] Sketch009
  AttachmentOffset = pos=(0,0,50.8) rot=(0,0,1;0rad)
  MapMode = 5
  Placement = pos=(50.8,-1.13e-14,1.13e-14) rot=(0.57735,0.57735,0.57735;2.0944rad)
  Support = -> [YZ_Plane008]
  sketch-geometry (8):
    g0: ArcOfCircle CenterX=-131 CenterY=25.4 CenterZ=0 NormalX=0 NormalY=0 NormalZ=1 AngleXU=0 Radius=5 StartAngle=1.5708 EndAngle=4.71239
    g1: ArcOfCircle CenterX=-95 CenterY=25.4 CenterZ=0 NormalX=0 NormalY=0 NormalZ=1 AngleXU=0 Radius=5 StartAngle=4.71239 EndAngle=7.85398
    g2: LineSegment StartX=-131 StartY=20.4 StartZ=0 EndX=-95 EndY=20.4 EndZ=0
    g3: LineSegment StartX=-131 StartY=30.4 StartZ=0 EndX=-95 EndY=30.4 EndZ=0
    g4: ArcOfCircle CenterX=95 CenterY=25.4 CenterZ=0 NormalX=0 NormalY=0 NormalZ=1 AngleXU=0 Radius=5 StartAngle=1.5708 EndAngle=4.71239
    g5: ArcOfCircle CenterX=131 CenterY=25.4 CenterZ=0 NormalX=0 NormalY=0 NormalZ=1 AngleXU=0 Radius=5 StartAngle=4.71239 EndAngle=7.85398
    g6: LineSegment StartX=95 StartY=20.4 StartZ=0 EndX=131 EndY=20.4 EndZ=0
    g7: LineSegment StartX=95 StartY=30.4 StartZ=0 EndX=131 EndY=30.4 EndZ=0
  constraints (18):
    c: Tangent(g0,g3) = 1.5708
    c: Tangent(g0,g2) = -1.5708
    c: Tangent(g2,g1) = -1.5708
    c: Tangent(g3,g1) = 1.5708
    c: Horizontal(g2)
    c: Equal(g0,g1)
    c: Tangent(g4,g7) = 1.5708
    c: Tangent(g4,g6) = -1.5708
    c: Tangent(g6,g5) = -1.5708
    c: Tangent(g7,g5) = 1.5708
    c: Horizontal(g6)
    c: Symmetric(g4,g1,g-2)
    c: Equal(g4,g1)
    c: Symmetric(g5,g0,g-2)
    c: Diameter(g1) = 10
    c: DistanceY(g-1,g4) = 25.4
    c: DistanceX(g0,g5) = 262
    c: DistanceX(g1,g4) = 190
FEATURE [PartDesign::Pocket] Pocket003
  AllowMultiFace = false
  BaseFeature = -> Pocket002
  Length = 5
  Length2 = 100
  Placement = pos=(0,0,0) rot=(1,0,0;1.5708rad)
  Profile = -> Sketch009
  Type = 2
FEATURE [PartDesign::Pocket] Pocket004
  AllowMultiFace = false
  BaseFeature = -> Pocket003
  Length = 5
  Length2 = 100
  Placement = pos=(0,0,0) rot=(1,0,0;1.5708rad)
  Profile = -> Sketch010
  Type = 2
FEATURE [PartDesign::Pocket] Pocket005
  AllowMultiFace = false
  BaseFeature = -> Pocket004
  Length = 35
  Length2 = 100
  Placement = pos=(0,0,0) rot=(1,0,0;1.5708rad)
  Profile = -> Sketch011
  Reversed = true
  Type = 0
FEATURE [PartDesign::Body] Body005
  Group = -> [Sketch008,Pad005,Sketch007,Pocket002,Sketch009,Pocket003,Sketch010,Pocket004,Sketch011,Pocket005]
  Origin = -> Origin010
  Tip = -> Pocket005
FEATURE [PartDesign::CoordinateSystem] LCS_1
  AttacherType = Attacher::AttachEngine3D
  AttachmentOffset = pos=(25.4,0,0) rot=(0,0,1;0rad)
  MapMode = 45
  Placement = pos=(25.4,-152.4,1.8e-15) rot=(0.57735,0.57735,0.57735;2.0944rad)
  Support = -> [Pocket005]
  expr: .AttachmentOffset.Base.x = 1"
FEATURE [PartDesign::CoordinateSystem] LCS_2
  AttacherType = Attacher::AttachEngine3D
  AttachmentOffset = pos=(-25.4,0,0) rot=(0,0,1;0rad)
  MapMode = 45
  Placement = pos=(25.4,152.4,1.8e-15) rot=(0.57735,0.57735,0.57735;2.0944rad)
  Support = -> [Pocket005]
  expr: .AttachmentOffset.Base.x = -1"
FEATURE [PartDesign::CoordinateSystem] LCS_3
  AttacherType = Attacher::AttachEngine3D
  MapMode = 11
  Placement = pos=(25.4,0,50.8) rot=(0,0,1;1.5708rad)
  Support = -> [Pocket005]
FEATURE [App::Part] Part007  label="frame_top_piece"
  Group = -> [Body005,LCS_1,LCS_2,LCS_3]
  Origin = -> Origin008
---- part z_motor_adaptor_plate.FCStd = doc fcstd_c9ba5154c790 ----
FCSTD DOCUMENT  (FreeCAD 0.19R23578 (Git))
Label: z_motor_adaptor_plate
License: All rights reserved
LicenseURL: http://en.wikipedia.org/wiki/All_rights_reserved
objects: TechDraw::DrawViewDimension×6, PartDesign::CoordinateSystem×4, Sketcher::SketchObject×2, TechDraw::DrawViewDimExtent×2, PartDesign::Pad×1, PartDesign::Pocket×1, PartDesign::Body×1, TechDraw::DrawSVGTemplate×1, TechDraw::DrawProjGroupItem×1, TechDraw::DrawProjGroup×1, TechDraw::DrawPage×1, App::Part×1
note: 11 computed .brp shape members not serialized (recipe doc carries the construction recipe); baked Part::Feature solids carry a one-line shape summary decoded from their .brp

FEATURE [Sketcher::SketchObject] Sketch093
  MapMode = 5
  Support = -> [XY_Plane105]
  expr: Constraints[43] = 60
  sketch-geometry (23):
    g0: LineSegment StartX=-34.6372 StartY=4.33805 StartZ=0 EndX=-20.1372 EndY=19.838 EndZ=0
    g1: LineSegment StartX=-15.5 StartY=21.85 StartZ=0 EndX=15.5 EndY=21.85 EndZ=0
    g2: LineSegment StartX=20.1372 StartY=19.838 StartZ=0 EndX=34.6372 EndY=4.33805 EndZ=0
    g3: LineSegment StartX=34.6372 StartY=-4.33805 StartZ=0 EndX=20.1372 EndY=-19.838 EndZ=0
    g4: LineSegment StartX=15.5 StartY=-21.85 StartZ=0 EndX=-15.5 EndY=-21.85 EndZ=0
    g5: LineSegment StartX=-20.1372 StartY=-19.838 StartZ=0 EndX=-34.6372 EndY=-4.33805 EndZ=0
    g6: ArcOfCircle CenterX=-30 CenterY=0 CenterZ=0 NormalX=0 NormalY=0 NormalZ=1 AngleXU=0 Radius=6.35 StartAngle=2.38952 EndAngle=3.89367
    g7: ArcOfCircle CenterX=-15.5 CenterY=15.5 CenterZ=0 NormalX=0 NormalY=0 NormalZ=1 AngleXU=0 Radius=6.35 StartAngle=1.5708 EndAngle=2.38952
    g8: ArcOfCircle CenterX=15.5 CenterY=15.5 CenterZ=0 NormalX=0 NormalY=0 NormalZ=1 AngleXU=0 Radius=6.35 StartAngle=0.752077 EndAngle=1.5708
    g9: ArcOfCircle CenterX=30 CenterY=0 CenterZ=0 NormalX=0 NormalY=0 NormalZ=1 AngleXU=0 Radius=6.35 StartAngle=5.53111 EndAngle=7.03526
    g10: ArcOfCircle CenterX=15.5 CenterY=-15.5 CenterZ=0 NormalX=0 NormalY=0 NormalZ=1 AngleXU=0 Radius=6.35 StartAngle=4.71239 EndAngle=5.53111
    g11: ArcOfCircle CenterX=-15.5 CenterY=-15.5 CenterZ=0 NormalX=0 NormalY=0 NormalZ=1 AngleXU=0 Radius=6.35 StartAngle=3.89367 EndAngle=4.71239
    g12: LineSegment StartX=-15.5 StartY=15.5 StartZ=0 EndX=15.5 EndY=15.5 EndZ=0
    g13: LineSegment StartX=15.5 StartY=15.5 StartZ=0 EndX=15.5 EndY=-15.5 EndZ=0
    g14: LineSegment StartX=15.5 StartY=-15.5 StartZ=0 EndX=-15.5 EndY=-15.5 EndZ=0
    g15: LineSegment StartX=-15.5 StartY=-15.5 StartZ=0 EndX=-15.5 EndY=15.5 EndZ=0
    g16: Circle CenterX=-15.5 CenterY=15.5 CenterZ=0 NormalX=0 NormalY=0 NormalZ=1 AngleXU=0 Radius=1.75
    g17: Circle CenterX=15.5 CenterY=15.5 CenterZ=0 NormalX=0 NormalY=0 NormalZ=1 AngleXU=0 Radius=1.75
    g18: Circle CenterX=15.5 CenterY=-15.5 CenterZ=0 NormalX=0 NormalY=0 NormalZ=1 AngleXU=0 Radius=1.75
    g19: Circle CenterX=-15.5 CenterY=-15.5 CenterZ=0 NormalX=0 NormalY=0 NormalZ=1 AngleXU=0 Radius=1.75
    g20: Circle CenterX=-30 CenterY=0 CenterZ=0 NormalX=0 NormalY=0 NormalZ=1 AngleXU=0 Radius=2.75
    g21: Circle CenterX=30 CenterY=0 CenterZ=0 NormalX=0 NormalY=0 NormalZ=1 AngleXU=0 Radius=2.75
    g22: Circle CenterX=0 CenterY=0 CenterZ=0 NormalX=0 NormalY=0 NormalZ=1 AngleXU=0 Radius=11.5
  constraints (49):
    c: Tangent(g0,g6) = 1.5708
    c: Tangent(g5,g6) = 1.5708
    c: Tangent(g0,g7) = 1.5708
    c: Tangent(g1,g7) = 1.5708
    c: Tangent(g1,g8) = 1.5708
    c: Tangent(g2,g8) = 1.5708
    c: Tangent(g2,g9) = 1.5708
    c: Tangent(g3,g9) = 1.5708
    c: Tangent(g3,g10) = 1.5708
    c: Tangent(g4,g10) = 1.5708
    c: Tangent(g4,g11) = 1.5708
    c: Tangent(g5,g11) = 1.5708
    c: Coincident(g12,g13)
    c: Coincident(g13,g14)
    c: Coincident(g14,g15)
    c: Coincident(g15,g12)
    c: Horizontal(g14)
    c: Vertical(g15)
    c: Coincident(g16,g12)
    c: Coincident(g17,g12)
    c: Coincident(g18,g13)
    c: Coincident(g19,g14)
    c: Equal(g16,g17)
    c: Equal(g17,g18)
    c: Equal(g18,g19)
    c: Diameter(g17) = 3.5
    c: Equal(g7,g6)
    c: Equal(g6,g11)
    c: Equal(g11,g10)
    c: Equal(g10,g8)
    c: Equal(g8,g9)
    c: Radius(g9) = 6.35
    c: Symmetric(g1,g4,g-1)
    c: Symmetric(g9,g6,g-2)
    c: Coincident(g20,g6)
    c: Coincident(g21,g9)
    c: PointOnObject(g6,g-1)
    c: Symmetric(g1,g1,g-2)
    c: Symmetric(g4,g4,g-2)
    c: Symmetric(g18,g17,g-1)
    c: Symmetric(g17,g16,g-2)
    c: Equal(g12,g13)
    c: DistanceX(g12,g12) = 31
    c: DistanceX(g6,g9) = 60
    c: Coincident(g8,g17)
    c: Coincident(g22,g-1)
    c: Diameter(g22) = 23
    c: Equal(g20,g21)
    c: Diameter(g21) = 5.5
FEATURE [PartDesign::Pad] Pad032  label="Pad033"
  Direction = (1,1,1)
  Length = 6.35
  Length2 = 100
  Profile = -> Sketch093
  Type = 0
FEATURE [Sketcher::SketchObject] Sketch094
  MapMode = 5
  Support = -> [XY_Plane105]
  sketch-geometry (8):
    g0: LineSegment StartX=-15.5 StartY=15.5 StartZ=0 EndX=15.5 EndY=15.5 EndZ=0
    g1: LineSegment StartX=15.5 StartY=15.5 StartZ=0 EndX=15.5 EndY=-15.5 EndZ=0
    g2: LineSegment StartX=15.5 StartY=-15.5 StartZ=0 EndX=-15.5 EndY=-15.5 EndZ=0
    g3: LineSegment StartX=-15.5 StartY=-15.5 StartZ=0 EndX=-15.5 EndY=15.5 EndZ=0
    g4: Circle CenterX=-15.5 CenterY=15.5 CenterZ=0 NormalX=0 NormalY=0 NormalZ=1 AngleXU=0 Radius=3
    g5: Circle CenterX=15.5 CenterY=15.5 CenterZ=0 NormalX=0 NormalY=0 NormalZ=1 AngleXU=0 Radius=3
    g6: Circle CenterX=15.5 CenterY=-15.5 CenterZ=0 NormalX=0 NormalY=0 NormalZ=1 AngleXU=0 Radius=3
    g7: Circle CenterX=-15.5 CenterY=-15.5 CenterZ=0 NormalX=0 NormalY=0 NormalZ=1 AngleXU=0 Radius=3
  constraints (18):
    c: Coincident(g0,g1)
    c: Coincident(g1,g2)
    c: Coincident(g2,g3)
    c: Coincident(g3,g0)
    c: Horizontal(g2)
    c: Vertical(g3)
    c: Coincident(g4,g0)
    c: Coincident(g5,g0)
    c: Coincident(g6,g1)
    c: Coincident(g7,g2)
    c: Equal(g5,g4)
    c: Equal(g4,g7)
    c: Equal(g7,g6)
    c: Diameter(g5) = 6
    c: Symmetric(g5,g6,g-1)
    c: Symmetric(g5,g4,g-2)
    c: DistanceX(g0,g0) = 31
    c: Equal(g3,g0)
FEATURE [PartDesign::Pocket] Pocket027
  BaseFeature = -> Pad032
  Length = 3
  Length2 = 100
  Profile = -> Sketch094
  Reversed = true
  Type = 0
FEATURE [PartDesign::Body] Body036  label="Body"
  Group = -> [Sketch093,Pad032,Sketch094,Pocket027]
  Origin = -> Origin105
  Tip = -> Pocket027
FEATURE [TechDraw::DrawSVGTemplate] Template010
  EditableTexts = Author=Alex Neufeld; DWG_num=2020-112; Date=11/07/2020; Revision=1; Scale=NTS; Subtitle=1 Req; Title=Z Axis Motor Bracket
  Height = 215.9
  Orientation = 1
  Width = 279.4
FEATURE [TechDraw::DrawProjGroupItem] ProjItem036  label="Front011"
  CoarseView = false
  Direction = (0,0,1)
  Focus = 100
  HardHidden = false
  IsoCount = 0
  IsoHidden = false
  IsoVisible = false
  LockPosition = true
  Perspective = false
  Rotation = 90
  RotationVector = (1,0,0)
  ScaleType = 2
  SeamHidden = false
  SeamVisible = true
  SmoothHidden = false
  SmoothVisible = true
  Source = -> [Body036]
  Type = 0
  X = 0
  XDirection = (1e-16,1,0)
  Y = 0
FEATURE [TechDraw::DrawProjGroup] ProjGroup011
  Anchor = -> ProjItem036
  AutoDistribute = true
  LockPosition = false
  ProjectionType = 0
  Rotation = 0
  ScaleType = 0
  Source = -> [Body036]
  Views = -> [ProjItem036]
  X = 139.7
  Y = 107.95
  spacingX = 15
  spacingY = 15
FEATURE [TechDraw::DrawViewDimExtent] DimExtent013
  Arbitrary = false
  ArbitraryTolerances = false
  CosmeticTags = b4d62288-45a0-4493-b462-dada78fb5f72 | ba20ee15-e9d9-4cfa-af9a-7a2251a67fee
  DirExtent = 0
  FormatSpec = %.3f
  FormatSpecOverTolerance = %+.2f
  FormatSpecUnderTolerance = %+.2f
  Inverted = false
  LockPosition = false
  MeasureType = 1
  OverTolerance = 0
  References2D = -> [ProjItem036]
  Rotation = 0
  ScaleType = 0
  Source = -> [ProjItem036]
  TheoreticalExact = false
  Type = 1
  UnderTolerance = 0
  X = 2.15719
  Y = 33.0755
FEATURE [TechDraw::DrawViewDimExtent] DimExtent014
  Arbitrary = false
  ArbitraryTolerances = false
  CosmeticTags = 38caeeea-741a-4d1c-8500-c1ebbf708ce5 | 3d63ee3c-2b32-485c-9a31-cd0c80d53145
  DirExtent = 1
  FormatSpec = %.3f
  FormatSpecOverTolerance = %+.2f
  FormatSpecUnderTolerance = %+.2f
  Inverted = false
  LockPosition = false
  MeasureType = 1
  OverTolerance = 0
  References2D = -> [ProjItem036]
  Rotation = 0
  ScaleType = 0
  Source = -> [ProjItem036]
  TheoreticalExact = false
  Type = 2
  UnderTolerance = 0
  X = 41.7766
  Y = -0.503435
FEATURE [TechDraw::DrawViewDimension] Dimension179
  Arbitrary = false
  ArbitraryTolerances = false
  FormatSpec = %.3f
  FormatSpecOverTolerance = %+.2f
  FormatSpecUnderTolerance = %+.2f
  Inverted = false
  LockPosition = false
  MeasureType = 1
  OverTolerance = 0
  References2D = -> [ProjItem036]
  Rotation = 0
  ScaleType = 0
  TheoreticalExact = false
  Type = 1
  UnderTolerance = 0
  X = -0.34372
  Y = -37.8094
FEATURE [TechDraw::DrawViewDimension] Dimension180
  Arbitrary = false
  ArbitraryTolerances = false
  FormatSpec = ⌀%.3f
  FormatSpecOverTolerance = %+.2f
  FormatSpecUnderTolerance = %+.2f
  Inverted = false
  LockPosition = false
  MeasureType = 1
  OverTolerance = 0
  References2D = -> [ProjItem036]
  Rotation = 0
  ScaleType = 0
  TheoreticalExact = false
  Type = 5
  UnderTolerance = 0
  X = -69.6032
  Y = 2.5779
FEATURE [TechDraw::DrawViewDimension] Dimension181
  Arbitrary = false
  ArbitraryTolerances = false
  FormatSpec = ⌀%.3f
  FormatSpecOverTolerance = %+.2f
  FormatSpecUnderTolerance = %+.2f
  Inverted = false
  LockPosition = false
  MeasureType = 1
  OverTolerance = 0
  References2D = -> [ProjItem036]
  Rotation = 0
  ScaleType = 0
  TheoreticalExact = false
  Type = 5
  UnderTolerance = 0
  X = -4.2965
  Y = 0.716083
FEATURE [TechDraw::DrawViewDimension] Dimension182
  Arbitrary = false
  ArbitraryTolerances = false
  FormatSpec = ⌀%.3f
  FormatSpecOverTolerance = %+.2f
  FormatSpecUnderTolerance = %+.2f
  Inverted = false
  LockPosition = false
  MeasureType = 1
  OverTolerance = 0
  References2D = -> [ProjItem036]
  Rotation = 0
  ScaleType = 0
  TheoreticalExact = false
  Type = 5
  UnderTolerance = 0
  X = 41.0745
  Y = 43.3087
FEATURE [TechDraw::DrawViewDimension] Dimension183
  Arbitrary = false
  ArbitraryTolerances = false
  FormatSpec = %.3f
  FormatSpecOverTolerance = %+.2f
  FormatSpecUnderTolerance = %+.2f
  Inverted = false
  LockPosition = false
  MeasureType = 1
  OverTolerance = 0
  References2D = -> [ProjItem036]
  Rotation = 0
  ScaleType = 0
  TheoreticalExact = false
  Type = 1
  UnderTolerance = 0
  X = -2.00503
  Y = -17.5364
FEATURE [TechDraw::DrawViewDimension] Dimension184
  Arbitrary = false
  ArbitraryTolerances = false
  FormatSpec = %.3f
  FormatSpecOverTolerance = %+.2f
  FormatSpecUnderTolerance = %+.2f
  Inverted = false
  LockPosition = false
  MeasureType = 1
  OverTolerance = 0
  References2D = -> [ProjItem036]
  Rotation = 0
  ScaleType = 0
  TheoreticalExact = false
  Type = 2
  UnderTolerance = 0
  X = -26.5951
  Y = 0.0656065
FEATURE [TechDraw::DrawPage] Page010  label="z_bracket_dwg"
  KeepUpdated = false
  NextBalloonIndex = 1
  ProjectionType = 0
  Template = -> Template010
  Views = -> [ProjGroup011,DimExtent013,DimExtent014,Dimension179,Dimension180,Dimension181,Dimension182,Dimension183,Dimension184]
FEATURE [PartDesign::CoordinateSystem] LCS_1
  AttacherType = Attacher::AttachEngine3D
  MapMode = 11
  Placement = pos=(0,0,0) rot=(0,0,1;1.5708rad)
  Support = -> [Pocket027]
FEATURE [PartDesign::CoordinateSystem] LCS_2
  AttacherType = Attacher::AttachEngine3D
  MapMode = 11
  Placement = pos=(0,0,6.35) rot=(0,0,1;1.5708rad)
  Support = -> [Pocket027]
FEATURE [PartDesign::CoordinateSystem] LCS_3
  AttacherType = Attacher::AttachEngine3D
  MapMode = 11
  Placement = pos=(-30,0,6.35) rot=(0,0,1;1.5708rad)
  Support = -> [Pocket027]
FEATURE [PartDesign::CoordinateSystem] LCS_4
  AttacherType = Attacher::AttachEngine3D
  MapMode = 11
  Placement = pos=(30,0,6.35) rot=(0,0,1;1.5708rad)
  Support = -> [Pocket027]
FEATURE [App::Part] Part  label="z_motor_adaptor_plate"
  Group = -> [Body036,LCS_1,LCS_2,LCS_3,LCS_4]
  Origin = -> Origin
